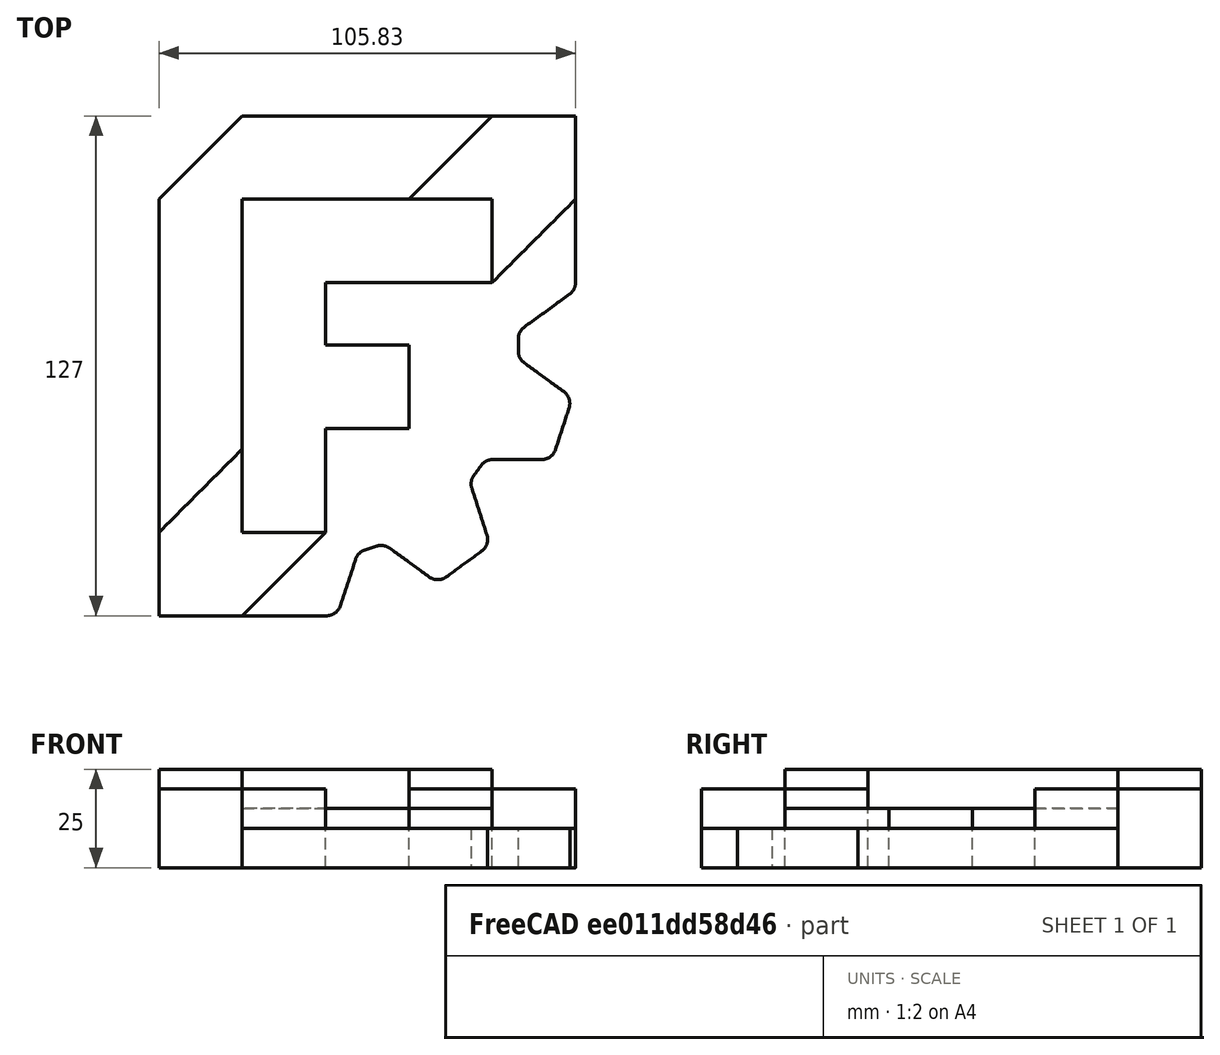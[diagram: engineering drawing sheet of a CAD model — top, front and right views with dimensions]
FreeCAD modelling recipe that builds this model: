
FCSTD DOCUMENT  (FreeCAD 1.0R39109 (Git))
Label: LOGO DE FREECAD EN FREECAD
License: All rights reserved
LicenseURL: https://en.wikipedia.org/wiki/All_rights_reserved
objects: Part::Feature×5, Sketcher::SketchObject×5, Part::Extrusion×5
note: 20 computed .brp shape members not serialized (recipe doc carries the construction recipe); baked Part::Feature solids carry a one-line shape summary decoded from their .brp

FEATURE [Part::Feature] path8_4
  shape: bbox 84.67 x 105.8 x 2e-07 mm, 1 faces, 0 solids (baked)
FEATURE [Part::Feature] path7_7
  shape: bbox 42.33 x 42.33 x 2e-07 mm, 1 faces, 0 solids (baked)
FEATURE [Part::Feature] path7_008
  shape: bbox 42.33 x 42.33 x 2e-07 mm, 1 faces, 0 solids (baked)
FEATURE [Part::Feature] path3_1
  shape: bbox 84.67 x 105.8 x 2e-07 mm, 1 faces, 0 solids (baked)
FEATURE [Part::Feature] path9_4
  shape: bbox 63.5 x 84.67 x 2e-07 mm, 1 faces, 0 solids (baked)
FEATURE [Sketcher::SketchObject] Sketch
  ArcFitTolerance = 1e-06
  FullyConstrained = false
  MakeInternals = false
  sketch-geometry (7):
    g0: BSplineCurve PolesCount=2 KnotsCount=2 Degree=1 IsPeriodic=0
    g1: BSplineCurve PolesCount=2 KnotsCount=2 Degree=1 IsPeriodic=0
    g2: BSplineCurve PolesCount=2 KnotsCount=2 Degree=1 IsPeriodic=0
    g3: BSplineCurve PolesCount=2 KnotsCount=2 Degree=1 IsPeriodic=0
    g4: BSplineCurve PolesCount=2 KnotsCount=2 Degree=1 IsPeriodic=0
    g5: BSplineCurve PolesCount=2 KnotsCount=2 Degree=1 IsPeriodic=0
    g6: BSplineCurve PolesCount=2 KnotsCount=2 Degree=1 IsPeriodic=0
  constraints (7):
    c: Coincident(g0,g1)
    c: Coincident(g1,g2)
    c: Coincident(g2,g3)
    c: Coincident(g3,g4)
    c: Coincident(g4,g5)
    c: Coincident(g5,g6)
    c: Coincident(g6,g0)
FEATURE [Sketcher::SketchObject] Sketch001
  ArcFitTolerance = 1e-06
  FullyConstrained = false
  MakeInternals = false
  sketch-geometry (6):
    g0: BSplineCurve PolesCount=2 KnotsCount=2 Degree=1 IsPeriodic=0
    g1: BSplineCurve PolesCount=2 KnotsCount=2 Degree=1 IsPeriodic=0
    g2: BSplineCurve PolesCount=2 KnotsCount=2 Degree=1 IsPeriodic=0
    g3: BSplineCurve PolesCount=2 KnotsCount=2 Degree=1 IsPeriodic=0
    g4: BSplineCurve PolesCount=2 KnotsCount=2 Degree=1 IsPeriodic=0
    g5: BSplineCurve PolesCount=2 KnotsCount=2 Degree=1 IsPeriodic=0
  constraints (6):
    c: Coincident(g0,g1)
    c: Coincident(g1,g2)
    c: Coincident(g2,g3)
    c: Coincident(g3,g4)
    c: Coincident(g4,g5)
    c: Coincident(g5,g0)
FEATURE [Sketcher::SketchObject] Sketch002
  ArcFitTolerance = 1e-06
  FullyConstrained = false
  MakeInternals = false
  sketch-geometry (10):
    g0: BSplineCurve PolesCount=2 KnotsCount=2 Degree=1 IsPeriodic=0
    g1: BSplineCurve PolesCount=2 KnotsCount=2 Degree=1 IsPeriodic=0
    g2: BSplineCurve PolesCount=2 KnotsCount=2 Degree=1 IsPeriodic=0
    g3: BSplineCurve PolesCount=2 KnotsCount=2 Degree=1 IsPeriodic=0
    g4: BSplineCurve PolesCount=2 KnotsCount=2 Degree=1 IsPeriodic=0
    g5: BSplineCurve PolesCount=2 KnotsCount=2 Degree=1 IsPeriodic=0
    g6: BSplineCurve PolesCount=2 KnotsCount=2 Degree=1 IsPeriodic=0
    g7: BSplineCurve PolesCount=2 KnotsCount=2 Degree=1 IsPeriodic=0
    g8: BSplineCurve PolesCount=2 KnotsCount=2 Degree=1 IsPeriodic=0
    g9: BSplineCurve PolesCount=2 KnotsCount=2 Degree=1 IsPeriodic=0
  constraints (10):
    c: Coincident(g0,g1)
    c: Coincident(g1,g2)
    c: Coincident(g2,g3)
    c: Coincident(g3,g4)
    c: Coincident(g4,g5)
    c: Coincident(g5,g6)
    c: Coincident(g6,g7)
    c: Coincident(g7,g8)
    c: Coincident(g8,g9)
    c: Coincident(g9,g0)
FEATURE [Sketcher::SketchObject] Sketch003
  ArcFitTolerance = 1e-06
  FullyConstrained = false
  MakeInternals = false
  sketch-geometry (6):
    g0: BSplineCurve PolesCount=2 KnotsCount=2 Degree=1 IsPeriodic=0
    g1: BSplineCurve PolesCount=2 KnotsCount=2 Degree=1 IsPeriodic=0
    g2: BSplineCurve PolesCount=2 KnotsCount=2 Degree=1 IsPeriodic=0
    g3: BSplineCurve PolesCount=2 KnotsCount=2 Degree=1 IsPeriodic=0
    g4: BSplineCurve PolesCount=2 KnotsCount=2 Degree=1 IsPeriodic=0
    g5: BSplineCurve PolesCount=2 KnotsCount=2 Degree=1 IsPeriodic=0
  constraints (6):
    c: Coincident(g0,g1)
    c: Coincident(g1,g2)
    c: Coincident(g2,g3)
    c: Coincident(g3,g4)
    c: Coincident(g4,g5)
    c: Coincident(g5,g0)
FEATURE [Sketcher::SketchObject] Sketch004
  ArcFitTolerance = 1e-06
  FullyConstrained = false
  MakeInternals = false
  sketch-geometry (33):
    g0: BSplineCurve PolesCount=2 KnotsCount=2 Degree=1 IsPeriodic=0
    g1: BSplineCurve PolesCount=2 KnotsCount=2 Degree=1 IsPeriodic=0
    g2: BSplineCurve PolesCount=2 KnotsCount=2 Degree=1 IsPeriodic=0
    g3: BSplineCurve PolesCount=2 KnotsCount=2 Degree=1 IsPeriodic=0
    g4: BSplineCurve PolesCount=2 KnotsCount=2 Degree=1 IsPeriodic=0
    g5: BSplineCurve PolesCount=2 KnotsCount=2 Degree=1 IsPeriodic=0
    g6: BSplineCurve PolesCount=2 KnotsCount=2 Degree=1 IsPeriodic=0
    g7: BSplineCurve PolesCount=2 KnotsCount=2 Degree=1 IsPeriodic=0
    g8: BSplineCurve PolesCount=2 KnotsCount=2 Degree=1 IsPeriodic=0
    g9: BSplineCurve PolesCount=4 KnotsCount=2 Degree=3 IsPeriodic=0
    g10: BSplineCurve PolesCount=2 KnotsCount=2 Degree=1 IsPeriodic=0
    g11: BSplineCurve PolesCount=4 KnotsCount=2 Degree=3 IsPeriodic=0
    g12: BSplineCurve PolesCount=2 KnotsCount=2 Degree=1 IsPeriodic=0
    g13: BSplineCurve PolesCount=4 KnotsCount=2 Degree=3 IsPeriodic=0
    g14: BSplineCurve PolesCount=2 KnotsCount=2 Degree=1 IsPeriodic=0
    g15: BSplineCurve PolesCount=4 KnotsCount=2 Degree=3 IsPeriodic=0
    g16: BSplineCurve PolesCount=2 KnotsCount=2 Degree=1 IsPeriodic=0
    g17: BSplineCurve PolesCount=4 KnotsCount=2 Degree=3 IsPeriodic=0
    g18: BSplineCurve PolesCount=2 KnotsCount=2 Degree=1 IsPeriodic=0
    g19: BSplineCurve PolesCount=4 KnotsCount=2 Degree=3 IsPeriodic=0
    g20: BSplineCurve PolesCount=2 KnotsCount=2 Degree=1 IsPeriodic=0
    g21: BSplineCurve PolesCount=4 KnotsCount=2 Degree=3 IsPeriodic=0
    g22: BSplineCurve PolesCount=2 KnotsCount=2 Degree=1 IsPeriodic=0
    g23: BSplineCurve PolesCount=4 KnotsCount=2 Degree=3 IsPeriodic=0
    g24: BSplineCurve PolesCount=2 KnotsCount=2 Degree=1 IsPeriodic=0
    g25: BSplineCurve PolesCount=4 KnotsCount=2 Degree=3 IsPeriodic=0
    g26: BSplineCurve PolesCount=2 KnotsCount=2 Degree=1 IsPeriodic=0
    g27: BSplineCurve PolesCount=4 KnotsCount=2 Degree=3 IsPeriodic=0
    g28: BSplineCurve PolesCount=2 KnotsCount=2 Degree=1 IsPeriodic=0
    g29: BSplineCurve PolesCount=4 KnotsCount=2 Degree=3 IsPeriodic=0
    g30: BSplineCurve PolesCount=2 KnotsCount=2 Degree=1 IsPeriodic=0
    g31: BSplineCurve PolesCount=4 KnotsCount=2 Degree=3 IsPeriodic=0
    g32: BSplineCurve PolesCount=2 KnotsCount=2 Degree=1 IsPeriodic=0
  constraints (33):
    c: Coincident(g0,g1)
    c: Coincident(g1,g2)
    c: Coincident(g2,g3)
    c: Coincident(g3,g4)
    c: Coincident(g4,g5)
    c: Coincident(g5,g6)
    c: Coincident(g6,g7)
    c: Coincident(g7,g8)
    c: Coincident(g8,g9)
    c: Coincident(g9,g10)
    c: Coincident(g10,g11)
    c: Coincident(g11,g12)
    c: Coincident(g12,g13)
    c: Coincident(g13,g14)
    c: Coincident(g14,g15)
    c: Coincident(g15,g16)
    c: Coincident(g16,g17)
    c: Coincident(g17,g18)
    c: Coincident(g18,g19)
    c: Coincident(g19,g20)
    c: Coincident(g20,g21)
    c: Coincident(g21,g22)
    c: Coincident(g22,g23)
    c: Coincident(g23,g24)
    c: Coincident(g24,g25)
    c: Coincident(g25,g26)
    c: Coincident(g26,g27)
    c: Coincident(g27,g28)
    c: Coincident(g28,g29)
    c: Coincident(g29,g30)
    c: Coincident(g30,g31)
    c: Coincident(g31,g32)
    c: Coincident(g32,g0)
FEATURE [Part::Extrusion] Extrude
  Base = -> Sketch
  Dir = (0,0,1)
  DirMode = 2
  FaceMakerClass = Part::FaceMakerBullseye
  FaceMakerMode = 3
  LengthFwd = 25
  LengthRev = 0
  Solid = true
  Symmetric = false
FEATURE [Part::Extrusion] Extrude001
  Base = -> Sketch001
  Dir = (0,0,1)
  DirMode = 2
  FaceMakerClass = Part::FaceMakerBullseye
  FaceMakerMode = 3
  LengthFwd = 20
  LengthRev = 0
  Solid = true
  Symmetric = false
FEATURE [Part::Extrusion] Extrude002
  Base = -> Sketch002
  Dir = (0,0,1)
  DirMode = 2
  FaceMakerClass = Part::FaceMakerBullseye
  FaceMakerMode = 3
  LengthFwd = 15
  LengthRev = 0
  Solid = true
  Symmetric = false
FEATURE [Part::Extrusion] Extrude003
  Base = -> Sketch003
  Dir = (0,0,1)
  DirMode = 2
  FaceMakerClass = Part::FaceMakerBullseye
  FaceMakerMode = 3
  LengthFwd = 20
  LengthRev = 0
  Solid = true
  Symmetric = false
FEATURE [Part::Extrusion] Extrude004
  Base = -> Sketch004
  Dir = (0,0,1)
  DirMode = 2
  FaceMakerClass = Part::FaceMakerBullseye
  FaceMakerMode = 3
  LengthFwd = 10
  LengthRev = 0
  Solid = true
  Symmetric = false
